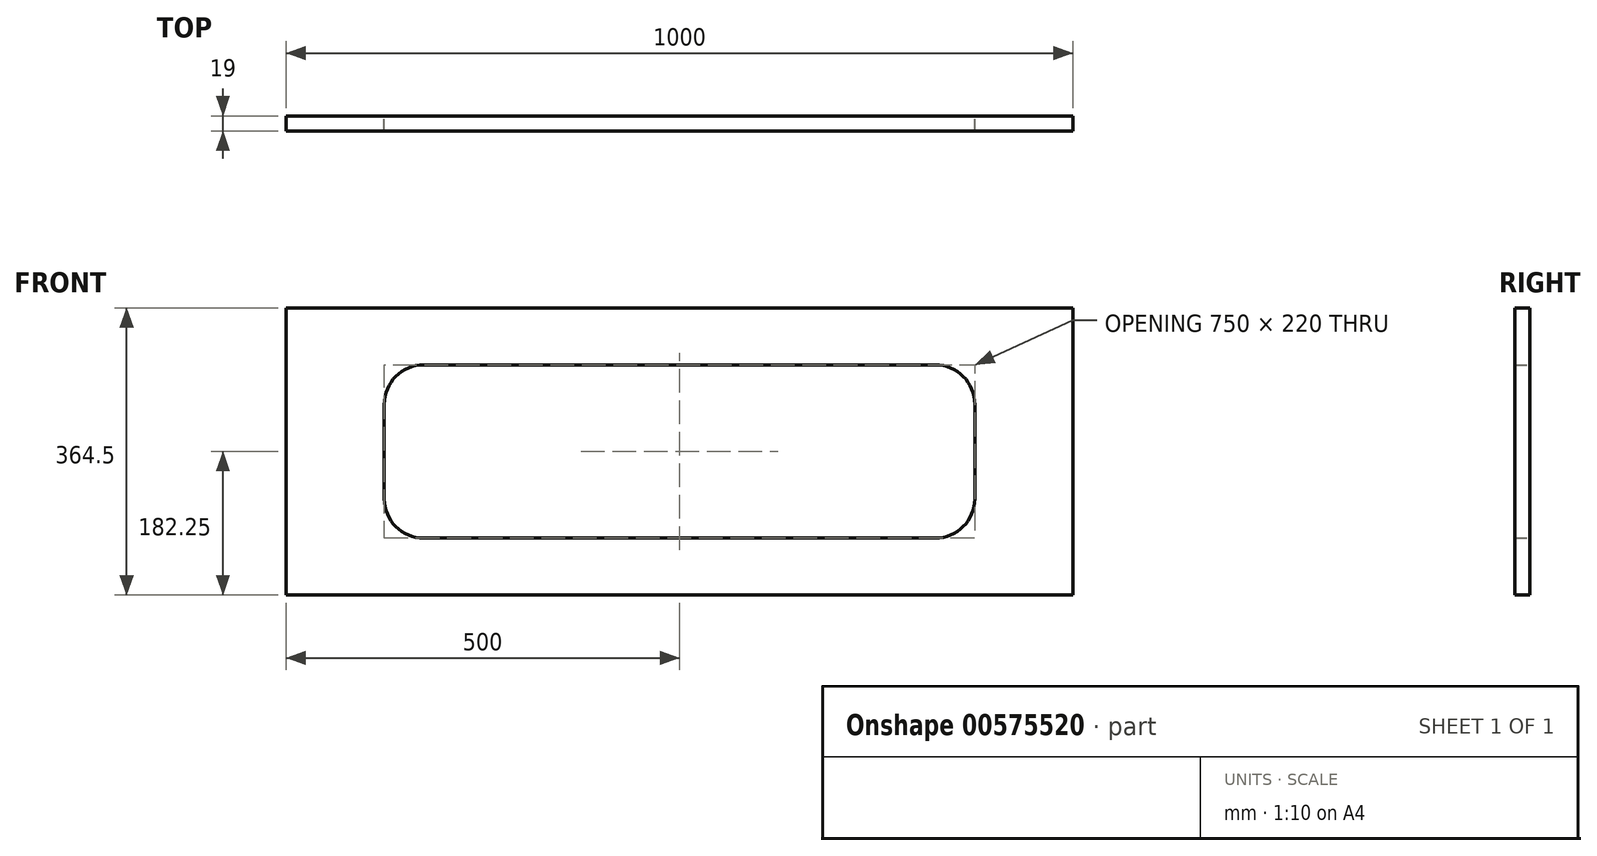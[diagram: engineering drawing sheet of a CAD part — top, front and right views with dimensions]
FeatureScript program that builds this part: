
annotation { "Feature Type Name" : "Feature", "Feature Type Description" : "" }
export const myFeature = defineFeature(function(context is Context, id is Id, definition is map)
    precondition{}
    {
        {
            var Q0;
            Q0=qCreatedBy(makeId("Front.planeOp"),FACE);
            var sketch = newSketch(context, id + "F0", { "sketchPlane" : qUnion([Q0])});
            skLineSegment(sketch, "E0.bottom", {"start": v(0, 0) * mm, "end": v(1000, 0) * mm, "construction": true});
            skLineSegment(sketch, "E0.left", {"start": v(0, 0) * mm, "end": v(0, 1590) * mm, "construction": true});
            skLineSegment(sketch, "E0.right", {"start": v(1000, 0) * mm, "end": v(1000, 1590) * mm, "construction": true});
            skLineSegment(sketch, "E1", {"start": v(500, 1590) * mm, "end": v(500, 0) * mm, "construction": true});
            skLineSegment(sketch, "E2.bottom", {"start": v(0, 1590) * mm, "end": v(1000, 1590) * mm, "construction": true});
            skLineSegment(sketch, "E2.left", {"start": v(0, 1590) * mm, "end": v(0, 290) * mm, "construction": true});
            skSolve(sketch);
        }
        {
            var Q0;
            Q0=qCreatedBy(makeId("Front.planeOp"),FACE);
            var sketch = newSketch(context, id + "F1", { "sketchPlane" : qUnion([Q0])});
            skLineSegment(sketch, "E3.bottom", {"start": v(0, 25) * mm, "end": v(1000, 25) * mm});
            skLineSegment(sketch, "E3.top", {"start": v(0, 389.5) * mm, "end": v(1000, 389.5) * mm});
            skLineSegment(sketch, "E3.left", {"start": v(0, 25) * mm, "end": v(0, 389.5) * mm});
            skLineSegment(sketch, "E3.right", {"start": v(1000, 25) * mm, "end": v(1000, 389.5) * mm});
            skLineSegment(sketch, "E4", {"start": v(0, 25) * mm, "end": v(1000, 25) * mm, "construction": true});
            skLineSegment(sketch, "E5.bottom", {"start": v(825, 317.25) * mm, "end": v(175, 317.25) * mm});
            skLineSegment(sketch, "E5.top", {"start": v(825, 97.25) * mm, "end": v(175, 97.25) * mm});
            skLineSegment(sketch, "E5.left", {"start": v(875, 267.25) * mm, "end": v(875, 147.25) * mm});
            skLineSegment(sketch, "E5.right", {"start": v(125, 267.25) * mm, "end": v(125, 147.25) * mm});
            skPoint(sketch, "E5.middle", {"position": v(500, 207.25) * mm});
            skLineSegment(sketch, "E6", {"start": v(0, 25) * mm, "end": v(1000, 389.5) * mm, "construction": true});
            skPoint(sketch, "E7.visualSharp", {"position": v(875, 317.25) * mm});
            skArc(sketch, "E8.filletArc", {"start": v(875, 267.25) * mm, "mid": v(860.36, 302.6) * mm, "end": v(825, 317.25) * mm});
            skPoint(sketch, "E9.visualSharp", {"position": v(875, 97.25) * mm});
            skArc(sketch, "E9.filletArc", {"start": v(825, 97.25) * mm, "mid": v(860.36, 111.9) * mm, "end": v(875, 147.25) * mm});
            skPoint(sketch, "E10.visualSharp", {"position": v(125, 97.25) * mm});
            skArc(sketch, "E10.filletArc", {"start": v(125, 147.25) * mm, "mid": v(139.64, 111.9) * mm, "end": v(175, 97.25) * mm});
            skPoint(sketch, "E11.visualSharp", {"position": v(125, 317.25) * mm});
            skArc(sketch, "E11.filletArc", {"start": v(175, 317.25) * mm, "mid": v(139.64, 302.6) * mm, "end": v(125, 267.25) * mm});
            skSolve(sketch);
        }
        {
            var Q0;
            Q0=makeQuery(id+"F1.imprint","IMPRINT",FACE,{"disambiguationData":[TD([[makeQuery(id+"F1.imprint","IMPRINT",EDGE,{"derivedFrom":sQuery(id+"F1.wireOp",EDGE,"E3.bottom")}),1.0]])]});
            extrude(context, id + "F2", {"entities" : qUnion([Q0]), "depth" : 19 * mm, "offsetDistance" : 25 * mm});
        }
        {
            var Q0;
            Q0=makeQuery(id+"F2.opExtrude","SWEPT_BODY",BODY,{"disambiguationData":[OSD([sQuery(id+"F1.wireOp",EDGE,"E3.bottom"),sQuery(id+"F1.wireOp",EDGE,"E3.top"),sQuery(id+"F1.wireOp",EDGE,"E3.left"),sQuery(id+"F1.wireOp",EDGE,"E3.right"),sQuery(id+"F1.wireOp",EDGE,"E5.bottom"),sQuery(id+"F1.wireOp",EDGE,"E5.top"),sQuery(id+"F1.wireOp",EDGE,"E5.left"),sQuery(id+"F1.wireOp",EDGE,"E5.right"),sQuery(id+"F1.wireOp",EDGE,"E8.filletArc"),sQuery(id+"F1.wireOp",EDGE,"E9.filletArc"),sQuery(id+"F1.wireOp",EDGE,"E10.filletArc"),sQuery(id+"F1.wireOp",EDGE,"E11.filletArc")])]});
            var Q1;
            Q1=makeQuery(id+"F2.opExtrude","CAP_VERTEX",VERTEX,{"disambiguationData":[OSD([sQuery(id+"F1.wireOp",EDGE,"E3.bottom"),sQuery(id+"F1.wireOp",EDGE,"E3.left")])],"isStart":false});
            var Q2;
            Q2=sQuery(id+"F0.wireOp",VERTEX,"E0.bottom.start");
            transform(context, id + "F3", {"entities" : qUnion([Q0]), "transformType" : TransformType.TRANSLATION_ENTITY, "oppositeDirectionEntity" : false, "transformLine" : qUnion([Q1, Q2]), "makeCopy" : false});
        }
        {
            var Q0;
            Q0=makeQuery(id+"F2.opExtrude","SWEPT_BODY",BODY,{"disambiguationData":[OSD([sQuery(id+"F1.wireOp",EDGE,"E3.bottom"),sQuery(id+"F1.wireOp",EDGE,"E3.top"),sQuery(id+"F1.wireOp",EDGE,"E3.left"),sQuery(id+"F1.wireOp",EDGE,"E3.right"),sQuery(id+"F1.wireOp",EDGE,"E5.bottom"),sQuery(id+"F1.wireOp",EDGE,"E5.top"),sQuery(id+"F1.wireOp",EDGE,"E5.left"),sQuery(id+"F1.wireOp",EDGE,"E5.right"),sQuery(id+"F1.wireOp",EDGE,"E8.filletArc"),sQuery(id+"F1.wireOp",EDGE,"E9.filletArc"),sQuery(id+"F1.wireOp",EDGE,"E10.filletArc"),sQuery(id+"F1.wireOp",EDGE,"E11.filletArc")])]});
            var Q1;
            Q1=makeQuery(id+"F2.opExtrude","CAP_VERTEX",VERTEX,{"disambiguationData":[OSD([sQuery(id+"F1.wireOp",EDGE,"E3.bottom"),sQuery(id+"F1.wireOp",EDGE,"E3.left")])],"isStart":true});
            var Q2;
            Q2=qCreatedBy(makeId("Origin.pointOp"),VERTEX);
            transform(context, id + "F4", {"entities" : qUnion([Q0]), "transformType" : TransformType.TRANSLATION_ENTITY, "oppositeDirectionEntity" : false, "transformLine" : qUnion([Q1, Q2]), "makeCopy" : false});
        }
    });
